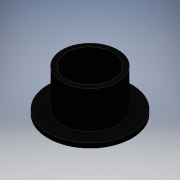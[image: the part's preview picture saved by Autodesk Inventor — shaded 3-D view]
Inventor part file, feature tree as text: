
AUTODESK INVENTOR PART (.ipt)
format: ipt  version: 2016 (Build 200138000, 138)  size: 103,424 bytes
history: native  units: mm
features: extrude x2, other x1, sketch x1
ambient origin geometry x8: Origin, YZ Plane, XZ Plane, XY Plane, X Axis, Y Axis, Z Axis, Center Point
bodies: Body1 (feature_tree)
feature tree (4):
  other  "ソリッド1"
  sketch  "スケッチ1"
  extrude  "押し出し1"  Depth=10.0mm
  extrude  "押し出し2"  Depth=12.0mm
